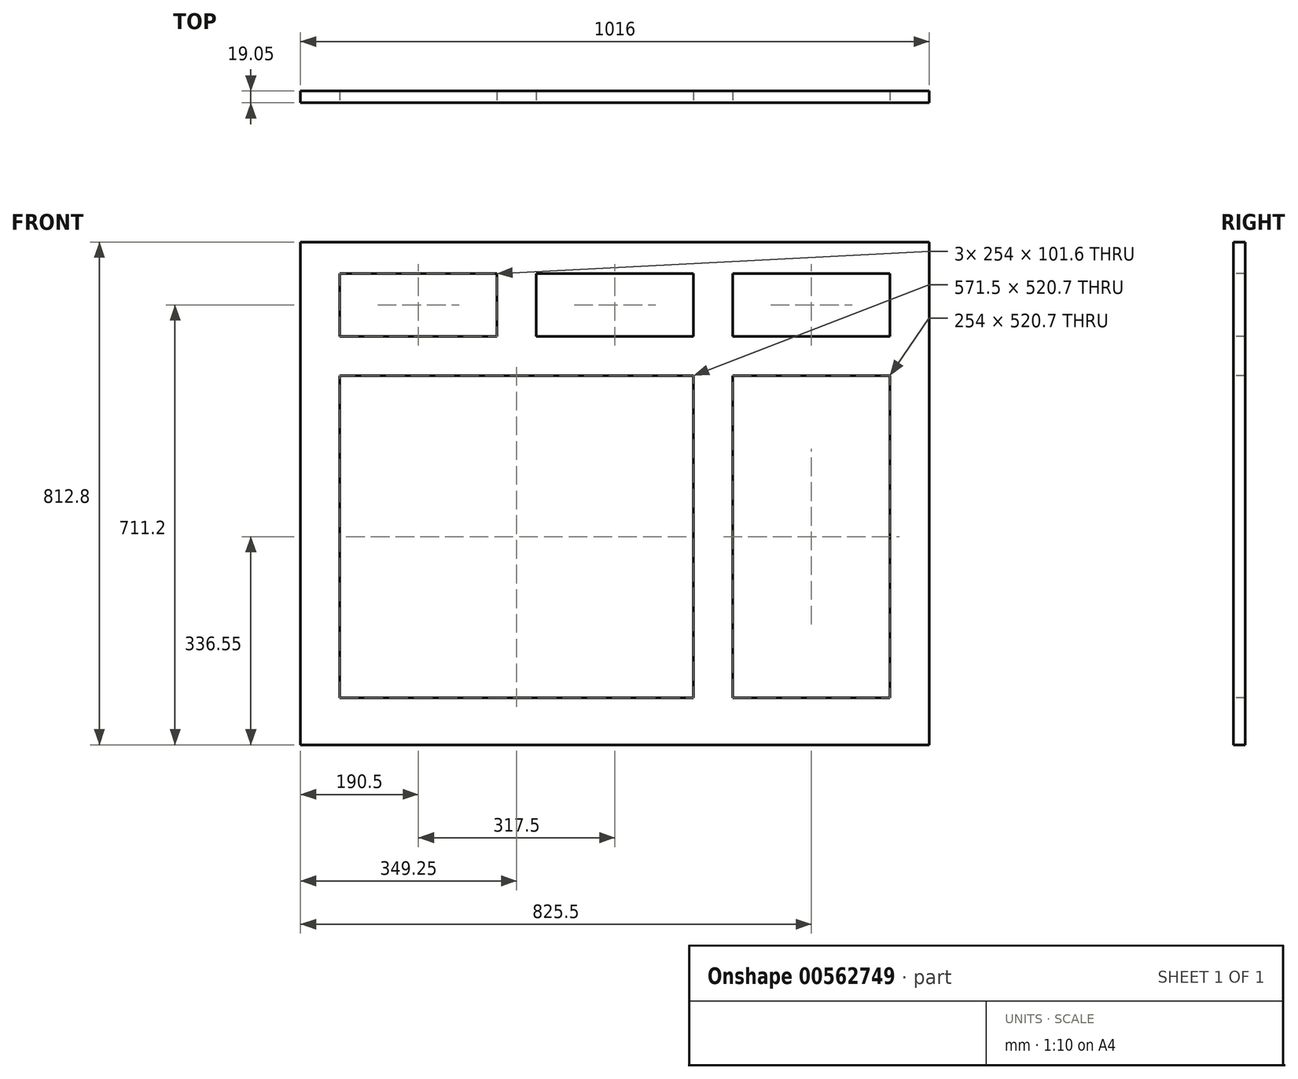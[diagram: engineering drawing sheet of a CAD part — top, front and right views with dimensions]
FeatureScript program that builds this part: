
annotation { "Feature Type Name" : "Feature", "Feature Type Description" : "" }
export const myFeature = defineFeature(function(context is Context, id is Id, definition is map)
    precondition{}
    {
        {
            var Q0;
            Q0=qCreatedBy(makeId("Front.planeOp"),FACE);
            var sketch = newSketch(context, id + "F0", { "sketchPlane" : qUnion([Q0])});
            skLineSegment(sketch, "E0.bottom", {"start": v(508, -406.4) * mm, "end": v(-508, -406.4) * mm});
            skLineSegment(sketch, "E0.top", {"start": v(508, 406.4) * mm, "end": v(-508, 406.4) * mm});
            skLineSegment(sketch, "E0.left", {"start": v(508, -406.4) * mm, "end": v(508, 406.4) * mm});
            skLineSegment(sketch, "E0.right", {"start": v(-508, -406.4) * mm, "end": v(-508, 406.4) * mm});
            skPoint(sketch, "E0.middle", {"position": v(0, 0) * mm});
            skSolve(sketch);
        }
        {
            var Q0;
            Q0 = qSketchRegion(id + "F0", true);
            extrude(context, id + "F1", {"entities" : qUnion([Q0]), "depth" : 19.05 * mm, "offsetDistance" : 25.4 * mm});
        }
        {
            var Q0;
            Q0=makeQuery(id+"F1.opExtrude","CAP_FACE",FACE,{"disambiguationData":[OSD([sQuery(id+"F0.wireOp",EDGE,"E0.bottom"),sQuery(id+"F0.wireOp",EDGE,"E0.top"),sQuery(id+"F0.wireOp",EDGE,"E0.left"),sQuery(id+"F0.wireOp",EDGE,"E0.right")])],"isStart":false});
            var sketch = newSketch(context, id + "F2", { "sketchPlane" : qUnion([Q0])});
            skLineSegment(sketch, "E1.bottom", {"start": v(-444.5, 355.6) * mm, "end": v(-190.5, 355.6) * mm});
            skLineSegment(sketch, "E1.top", {"start": v(-444.5, 254) * mm, "end": v(-190.5, 254) * mm});
            skLineSegment(sketch, "E1.left", {"start": v(-444.5, 355.6) * mm, "end": v(-444.5, 254) * mm});
            skLineSegment(sketch, "E1.right", {"start": v(-190.5, 355.6) * mm, "end": v(-190.5, 254) * mm});
            skLineSegment(sketch, "E2.bottom", {"start": v(-127, 355.6) * mm, "end": v(127, 355.6) * mm});
            skLineSegment(sketch, "E2.top", {"start": v(-127, 254) * mm, "end": v(127, 254) * mm});
            skLineSegment(sketch, "E2.left", {"start": v(-127, 355.6) * mm, "end": v(-127, 254) * mm});
            skLineSegment(sketch, "E2.right", {"start": v(127, 355.6) * mm, "end": v(127, 254) * mm});
            skLineSegment(sketch, "E3.bottom", {"start": v(190.5, 355.6) * mm, "end": v(444.5, 355.6) * mm});
            skLineSegment(sketch, "E3.top", {"start": v(190.5, 254) * mm, "end": v(444.5, 254) * mm});
            skLineSegment(sketch, "E3.left", {"start": v(190.5, 355.6) * mm, "end": v(190.5, 254) * mm});
            skLineSegment(sketch, "E3.right", {"start": v(444.5, 355.6) * mm, "end": v(444.5, 254) * mm});
            skLineSegment(sketch, "E4.bottom", {"start": v(-444.5, 190.5) * mm, "end": v(127, 190.5) * mm});
            skLineSegment(sketch, "E4.top", {"start": v(-444.5, -330.2) * mm, "end": v(127, -330.2) * mm});
            skLineSegment(sketch, "E4.left", {"start": v(-444.5, 190.5) * mm, "end": v(-444.5, -330.2) * mm});
            skLineSegment(sketch, "E4.right", {"start": v(127, 190.5) * mm, "end": v(127, -330.2) * mm});
            skLineSegment(sketch, "E5.bottom", {"start": v(190.5, 190.5) * mm, "end": v(444.5, 190.5) * mm});
            skLineSegment(sketch, "E5.top", {"start": v(190.5, -330.2) * mm, "end": v(444.5, -330.2) * mm});
            skLineSegment(sketch, "E5.left", {"start": v(190.5, 190.5) * mm, "end": v(190.5, -330.2) * mm});
            skLineSegment(sketch, "E5.right", {"start": v(444.5, 190.5) * mm, "end": v(444.5, -330.2) * mm});
            skSolve(sketch);
        }
        {
            var Q0;
            Q0=makeQuery(id+"F2.imprint","IMPRINT",FACE,{"disambiguationData":[TD([[makeQuery(id+"F2.imprint","IMPRINT",EDGE,{"derivedFrom":sQuery(id+"F2.wireOp",EDGE,"E3.bottom")}),-1.0]])]});
            var Q1;
            Q1=makeQuery(id+"F2.imprint","IMPRINT",FACE,{"disambiguationData":[TD([[makeQuery(id+"F2.imprint","IMPRINT",EDGE,{"derivedFrom":sQuery(id+"F2.wireOp",EDGE,"E2.bottom")}),-1.0]])]});
            var Q2;
            Q2=makeQuery(id+"F2.imprint","IMPRINT",FACE,{"disambiguationData":[TD([[makeQuery(id+"F2.imprint","IMPRINT",EDGE,{"derivedFrom":sQuery(id+"F2.wireOp",EDGE,"E1.bottom")}),-1.0]])]});
            var Q3;
            Q3=makeQuery(id+"F2.imprint","IMPRINT",FACE,{"disambiguationData":[TD([[makeQuery(id+"F2.imprint","IMPRINT",EDGE,{"derivedFrom":sQuery(id+"F2.wireOp",EDGE,"E4.bottom")}),-1.0]])]});
            var Q4;
            Q4=makeQuery(id+"F2.imprint","IMPRINT",FACE,{"disambiguationData":[TD([[makeQuery(id+"F2.imprint","IMPRINT",EDGE,{"derivedFrom":sQuery(id+"F2.wireOp",EDGE,"E5.bottom")}),-1.0]])]});
            extrude(context, id + "F3", {"entities" : qUnion([Q0, Q1, Q2, Q3, Q4]), "operationType" : NewBodyOperationType.REMOVE, "endBound" : BoundingType.THROUGH_ALL, "oppositeDirection" : true, "depth" : 25.4 * mm, "offsetDistance" : 25.4 * mm});
        }
    });
